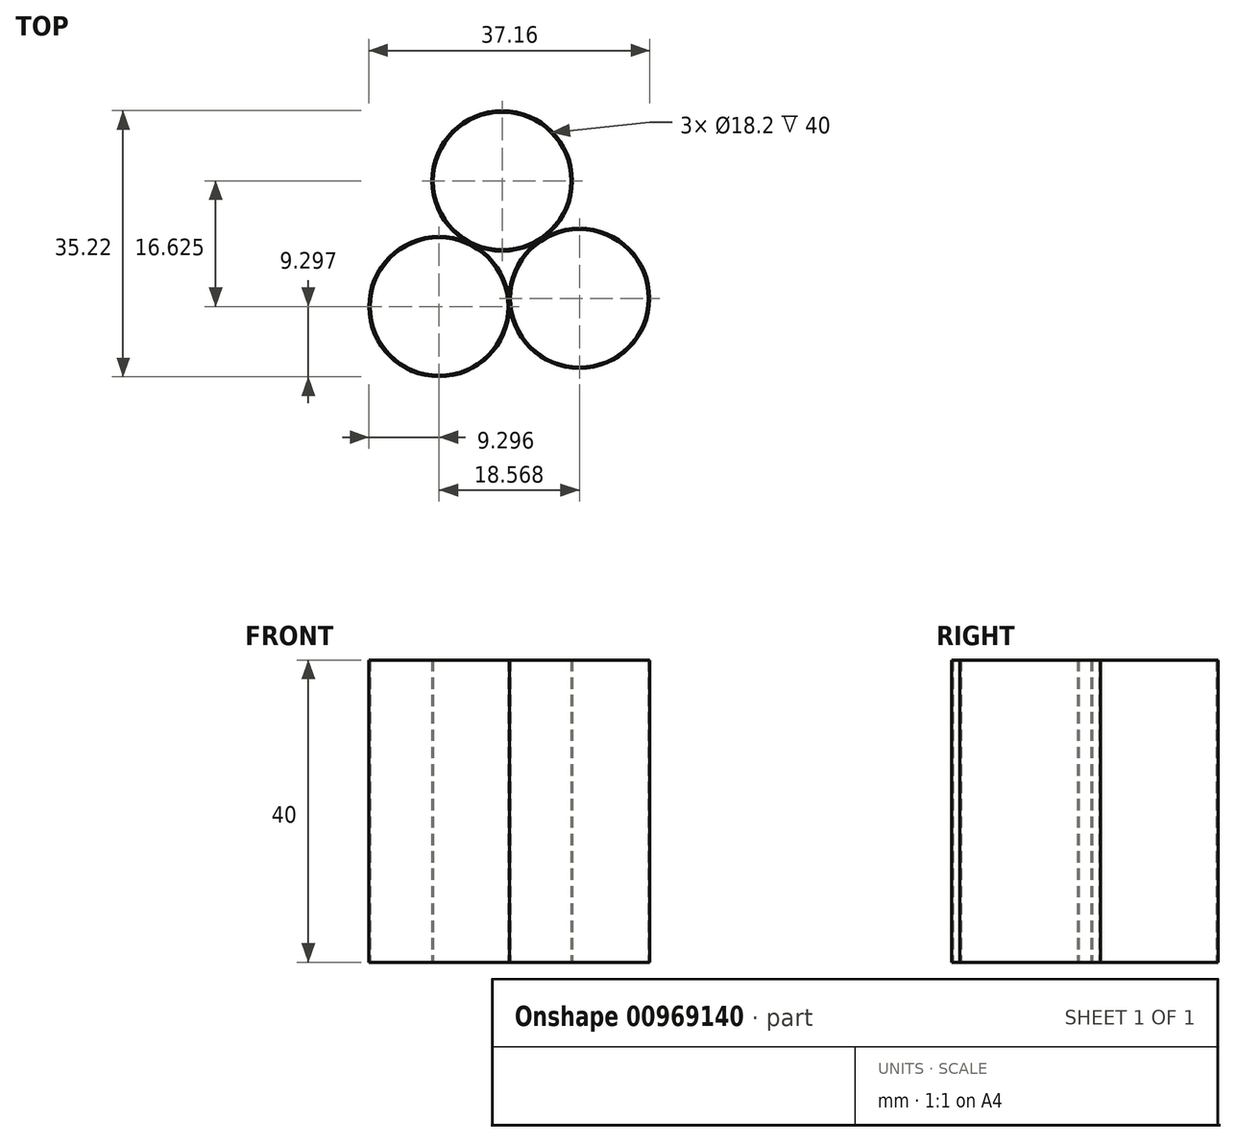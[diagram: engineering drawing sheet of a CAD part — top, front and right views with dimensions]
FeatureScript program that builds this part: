
annotation { "Feature Type Name" : "Feature", "Feature Type Description" : "" }
export const myFeature = defineFeature(function(context is Context, id is Id, definition is map)
    precondition{}
    {
        {
            var Q0;
            Q0=qCreatedBy(makeId("Top.planeOp"),FACE);
            var sketch = newSketch(context, id + "F0", { "sketchPlane" : qUnion([Q0])});
            skCircle(sketch, "E0", {"center": v(-31.6, 18.64) * mm, "radius": 9.1 * mm});
            skCircle(sketch, "E1.0", {"center": v(-31.6, 18.64) * mm, "radius": 9.3 * mm});
            skCircle(sketch, "E2", {"center": v(-13.04, 19.73) * mm, "radius": 9.1 * mm});
            skCircle(sketch, "E3.0", {"center": v(-13.04, 19.73) * mm, "radius": 9.3 * mm});
            skCircle(sketch, "E4", {"center": v(-23.26, 35.26) * mm, "radius": 9.1 * mm});
            skCircle(sketch, "E5.0", {"center": v(-23.26, 35.26) * mm, "radius": 9.3 * mm});
            skSolve(sketch);
        }
        {
            var Q0;
            Q0=makeQuery(id+"F0.imprint","IMPRINT",FACE,{"disambiguationData":[TD([[makeQuery(id+"F0.imprint","IMPRINT",EDGE,{"derivedFrom":sQuery(id+"F0.wireOp",EDGE,"E0")}),-1.0]])]});
            var Q1;
            Q1=makeQuery(id+"F0.imprint","IMPRINT",FACE,{"disambiguationData":[TD([[makeQuery(id+"F0.imprint","IMPRINT",EDGE,{"derivedFrom":sQuery(id+"F0.wireOp",EDGE,"E2")}),-1.0]])]});
            var Q2;
            Q2=makeQuery(id+"F0.imprint","IMPRINT",FACE,{"disambiguationData":[TD([[makeQuery(id+"F0.imprint","IMPRINT",EDGE,{"derivedFrom":sQuery(id+"F0.wireOp",EDGE,"E4")}),-1.0]])]});
            extrude(context, id + "F1", {"entities" : qUnion([Q0, Q1, Q2]), "depth" : 40 * mm, "offsetDistance" : 25 * mm});
        }
    });
